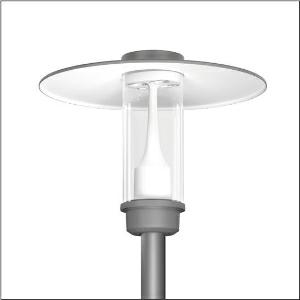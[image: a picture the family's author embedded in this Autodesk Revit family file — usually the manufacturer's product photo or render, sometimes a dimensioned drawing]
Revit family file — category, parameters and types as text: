
# Revit family: litepole_2_iq___p1_0a_5xa5425ff14h_a7e5
name_source: partatom
category: Lighting Fixtures
units: mm (PartAtom-declared; Revit-internal decimal feet)

## family parameters
Cut with Voids When Loaded = No
Host = Face
Light Source = No
Part Type = Normal
Room Calculation Point = No
Round Connector Dimension = Use Diameter
Shared = No

## types (1)
- --- (1 x LED, 1520 lm, 10.5 W, 3000K)
    Apparent Load = 11 VA
    CIE Flux Codes = 33 62 89 96 100
    Color Rendering = 70
    Color Temperature = 3000K
    Default Elevation = 1800 mm
    Description = Litepole 2 iQ, mast luminaire, Module 540 iQ-SR, primary light control with 3 zone facetted reflector, of plastic, silver coated, highly specular, structured, primary optical cover: cover, of PMMA, transparent, light distribution: P1.0a, light emission: direct distribution, primary light characteristic: strongly asymmetric, installation type: post-top, LED, High Power LED, rated luminous flux: 1.520lm, luminous efficacy: 145lm/W, light colour: 730, colour temperature: 3000K, control gear: ECG iQ, control: Auto-Match, Temp-Guard, Lumen-Switch, Night-Set, Smart-Wire, Light-Fading, Desk-Remote (wireless, voltage-free reading and setting of iQ features in the workshop via application-optimized NFC function/RFID function), optimised constant luminous flux control (CLO 2.0), Street-Remote, pre-setting: logarithmic dimming characteristic, with terminal, 6-pole, max. 2.5mm², mains connection: 230..240V, AC, 50/60Hz, start of lifetime: 11W, end of service life: 11W, reduction: 5W, luminaire housing, upper part, of aluminium, coated, Siteco® metallic grey (DB 702S), diameter: 750mm, height: 590mm, spigot size: d x l = 76 x 70mm (post-top) | with reducer (optional accessory) 60 x 70mm, post-top mast mounting element, of diecast aluminium, coated, Siteco® metallic grey (DB 702S), Module 540 iQ-SR, traffic white (RAL 9016), equipment: standard, protection rating (complete): IP65, insulation class (complete): insulation class II (safety insulation), certification: CE, ENEC, VDE, packaging unit: 1 piece

Light Distribution: P1.0a
    Height = 590 mm
    Lamp = 1 x LED
    Lamp Light Flux = 1520 lm
    Lamp Power = 10.5 W
    Lamp count = 1
    Length = 750 mm
    Luminous efficacy = 145 lm/W
    Manufacturer = Siteco
    ModVariant = No
    Model = 5XA5425FF14H
    Number of Poles = 1
    OnlyDefault = Yes
    Power Factor = 1
    Product Name = Litepole 2 iQ | P1.0a
    Product group = mast luminaire | pylon top
    ProductGroupID = 6100
    Protection Class = Protection class II
    Protection Degree = IP 65
    RLX_Detail_Level = 1
    RLX_Emergency_Light_Flux = 0 lm
    RLX_Emergency_Type = 0
    RLX_Emergency_Type_DB = No
    RlxData = <blob elided: 138149 chars, md5=32e28793>
    Socket = socket
    Standby Power = 0 W
    System Light Flux = 1520 lm
    System Power = 11 W
    Type Comments = factory setting: luminous flux: 100 % | dim-lin: 254 | 419 mA
    Type Image = l_1006518.jpg
    URL = http://relux.com
    VarID = @adj_165197
    Voltage = 0 V
    Weight = 0.00 kg
    Width = 0 mm  [stored 0 ft]

note: [stored X ft] marks values corroborated as IEEE doubles in the binary element streams (Revit-internal decimal feet)

## geometry (parser evidence)
native form markers: Blend x4, Sweep x9
no freeform markers — native parametric forms only
